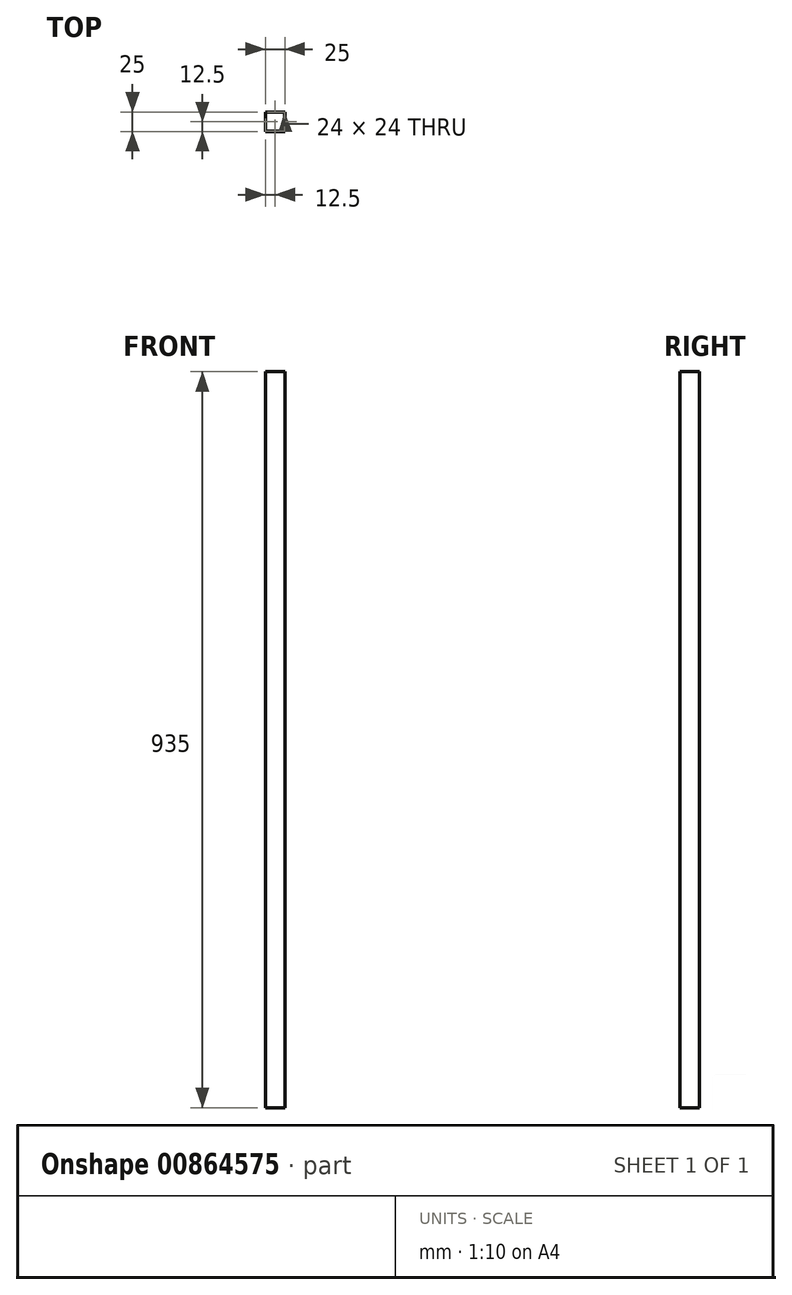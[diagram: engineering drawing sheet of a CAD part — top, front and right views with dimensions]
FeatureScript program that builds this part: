
annotation { "Feature Type Name" : "Feature", "Feature Type Description" : "" }
export const myFeature = defineFeature(function(context is Context, id is Id, definition is map)
    precondition{}
    {
        {
            var Q0;
            Q0=qCreatedBy(makeId("Top.planeOp"),FACE);
            var sketch = newSketch(context, id + "F0", { "sketchPlane" : qUnion([Q0])});
            skLineSegment(sketch, "E0.bottom", {"start": v(0, 0) * mm, "end": v(25, 0) * mm});
            skLineSegment(sketch, "E0.top", {"start": v(0, -25) * mm, "end": v(25, -25) * mm});
            skLineSegment(sketch, "E0.left", {"start": v(0, 0) * mm, "end": v(0, -25) * mm});
            skLineSegment(sketch, "E0.right", {"start": v(25, 0) * mm, "end": v(25, -25) * mm});
            skLineSegment(sketch, "E1.bottom", {"start": v(0.5, -0.5) * mm, "end": v(24.5, -0.5) * mm});
            skLineSegment(sketch, "E1.top", {"start": v(0.5, -24.5) * mm, "end": v(24.5, -24.5) * mm});
            skLineSegment(sketch, "E1.left", {"start": v(0.5, -0.5) * mm, "end": v(0.5, -24.5) * mm});
            skLineSegment(sketch, "E1.right", {"start": v(24.5, -0.5) * mm, "end": v(24.5, -24.5) * mm});
            skSolve(sketch);
        }
        {
            var Q0;
            Q0=makeQuery(id+"F0.imprint","IMPRINT",FACE,{"disambiguationData":[TD([[makeQuery(id+"F0.imprint","IMPRINT",EDGE,{"derivedFrom":sQuery(id+"F0.wireOp",EDGE,"E0.bottom")}),-1.0]])]});
            extrude(context, id + "F1", {"entities" : qUnion([Q0]), "depth" : 935 * mm, "offsetDistance" : 25 * mm});
        }
    });
